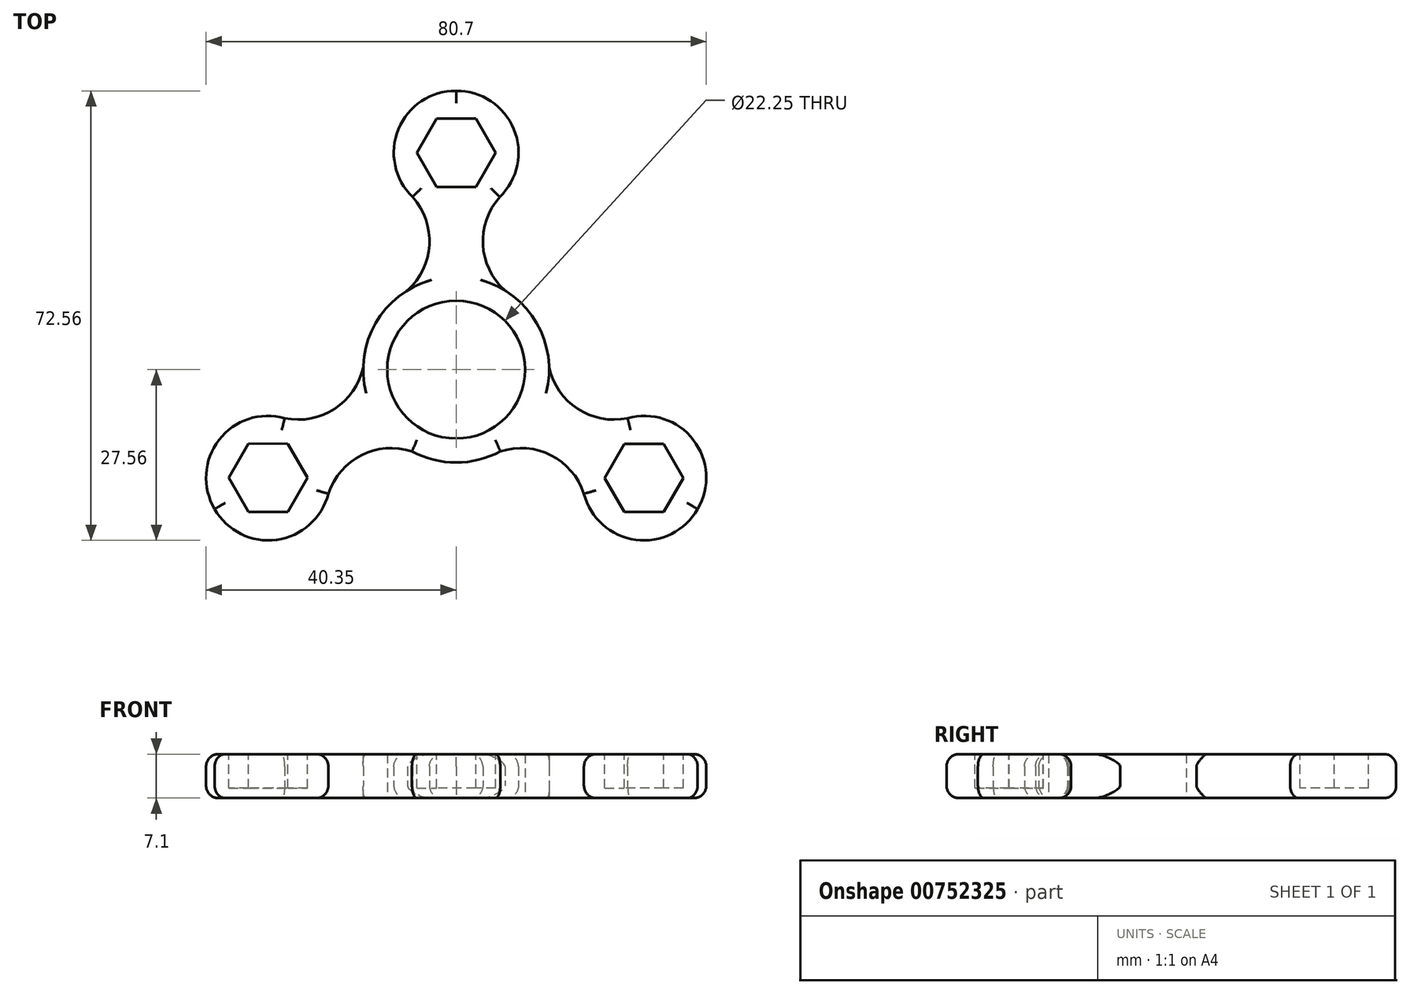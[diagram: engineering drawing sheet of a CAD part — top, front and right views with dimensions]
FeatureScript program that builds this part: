
annotation { "Feature Type Name" : "Feature", "Feature Type Description" : "" }
export const myFeature = defineFeature(function(context is Context, id is Id, definition is map)
    precondition{}
    {
        {
            var Q0;
            Q0=qCreatedBy(makeId("Top.planeOp"),FACE);
            var sketch = newSketch(context, id + "F0", { "sketchPlane" : qUnion([Q0])});
            skCircle(sketch, "E0", {"center": v(0, 0) * mm, "radius": 11.12 * mm});
            skCircle(sketch, "E1", {"center": v(0, 0) * mm, "radius": 15 * mm});
            skSolve(sketch);
        }
        {
            var Q0;
            Q0=qSketchRegion(id+"F0",true);
            extrude(context, id + "F1", {"entities" : qUnion([Q0]), "depth" : 7.1 * mm, "offsetDistance" : 25 * mm});
        }
        {
            var Q0;
            Q0=qCreatedBy(makeId("Top.planeOp"),FACE);
            var sketch = newSketch(context, id + "F2", { "sketchPlane" : qUnion([Q0])});
            skArc(sketch, "E2", {"start": v(7.04, 27.88) * mm, "mid": v(9.31, 38.82) * mm, "end": v(0, 45) * mm});
            skArc(sketch, "E3", {"start": v(7.04, 27.88) * mm, "mid": v(4.37, 19.6) * mm, "end": v(8.74, 12.07) * mm});
            skArc(sketch, "E4.MirrorCS", {"start": v(-7.04, 27.88) * mm, "mid": v(-9.31, 38.82) * mm, "end": v(0, 45) * mm});
            skArc(sketch, "E5.MirrorCS", {"start": v(-7.04, 27.88) * mm, "mid": v(-4.37, 19.6) * mm, "end": v(-8.74, 12.07) * mm});
            skArc(sketch, "E6", {"start": v(8.74, 12.07) * mm, "mid": v(0, 14.88) * mm, "end": v(-8.74, 12.07) * mm});
            skArc(sketch, "E7.1.0", {"start": v(-27.66, -7.84) * mm, "mid": v(-19.16, -6.01) * mm, "end": v(-14.82, 1.53) * mm});
            skArc(sketch, "E7.1.1", {"start": v(-20.62, -20.04) * mm, "mid": v(-14.78, -13.58) * mm, "end": v(-6.08, -13.6) * mm});
            skArc(sketch, "E7.1.2", {"start": v(-20.62, -20.04) * mm, "mid": v(-28.96, -27.47) * mm, "end": v(-38.97, -22.5) * mm});
            skArc(sketch, "E7.1.3", {"start": v(-27.66, -7.84) * mm, "mid": v(-38.27, -11.35) * mm, "end": v(-38.97, -22.5) * mm});
            skArc(sketch, "E7.1.4", {"start": v(-14.82, 1.53) * mm, "mid": v(-12.88, -7.44) * mm, "end": v(-6.08, -13.6) * mm});
            skArc(sketch, "E7.2.0", {"start": v(20.62, -20.04) * mm, "mid": v(14.78, -13.58) * mm, "end": v(6.08, -13.6) * mm});
            skArc(sketch, "E7.2.1", {"start": v(27.66, -7.84) * mm, "mid": v(19.16, -6.01) * mm, "end": v(14.82, 1.53) * mm});
            skArc(sketch, "E7.2.2", {"start": v(27.66, -7.84) * mm, "mid": v(38.27, -11.35) * mm, "end": v(38.97, -22.5) * mm});
            skArc(sketch, "E7.2.3", {"start": v(20.62, -20.04) * mm, "mid": v(28.96, -27.47) * mm, "end": v(38.97, -22.5) * mm});
            skArc(sketch, "E7.2.4", {"start": v(6.08, -13.6) * mm, "mid": v(12.88, -7.44) * mm, "end": v(14.82, 1.53) * mm});
            skPoint(sketch, "E7.center", {"position": v(0, 0) * mm});
            skSolve(sketch);
        }
        {
            var Q0;
            Q0=qSketchRegion(id+"F2",true);
            extrude(context, id + "F3", {"entities" : qUnion([Q0]), "operationType" : NewBodyOperationType.ADD, "depth" : 7.1 * mm, "offsetDistance" : 25 * mm});
        }
        {
            var Q0;
            Q0=makeQuery(id+"F3.opExtrude","CAP_EDGE",EDGE,{"disambiguationData":[OSD([sQuery(id+"F2.wireOp",EDGE,"E4.MirrorCS")])],"isStart":false});
            var Q1;
            Q1=makeQuery(id+"F3.opExtrude","CAP_EDGE",EDGE,{"disambiguationData":[OSD([sQuery(id+"F2.wireOp",EDGE,"E7.1.3")])],"isStart":false});
            var Q2;
            Q2=makeQuery(id+"F3.opExtrude","CAP_EDGE",EDGE,{"disambiguationData":[OSD([sQuery(id+"F2.wireOp",EDGE,"E7.2.3")])],"isStart":false});
            var Q3;
            {var subQ0=sQuery(id+"F0.wireOp",EDGE,"E1");var subQ1=sQuery(id+"F2.wireOp",EDGE,"E7.1.1");Q3=makeQuery(id+"F3.boolean.opBoolean","SPLIT",EDGE,{"disambiguationData":[TD([makeQuery(id+"F3.opExtrude","SWEPT_FACE",FACE,{"disambiguationData":[OSD([subQ1])]})])],"derivedFrom":makeQuery(id+"F1.opExtrude","CAP_EDGE",EDGE,{"disambiguationData":[OSD([subQ0])],"isStart":false})});}
            var Q4;
            {var subQ0=sQuery(id+"F2.wireOp",EDGE,"E3");var subQ1=sQuery(id+"F0.wireOp",EDGE,"E1");Q4=makeQuery(id+"F3.boolean.opBoolean","SPLIT",EDGE,{"disambiguationData":[TD([makeQuery(id+"F3.opExtrude","SWEPT_FACE",FACE,{"disambiguationData":[OSD([subQ0])]})])],"derivedFrom":makeQuery(id+"F1.opExtrude","CAP_EDGE",EDGE,{"disambiguationData":[OSD([subQ1])],"isStart":false})});}
            var Q5;
            {var subQ0=sQuery(id+"F2.wireOp",EDGE,"E5.MirrorCS");var subQ1=sQuery(id+"F0.wireOp",EDGE,"E1");Q5=makeQuery(id+"F3.boolean.opBoolean","SPLIT",EDGE,{"disambiguationData":[TD([makeQuery(id+"F3.opExtrude","SWEPT_FACE",FACE,{"disambiguationData":[OSD([subQ0])]})])],"derivedFrom":makeQuery(id+"F1.opExtrude","CAP_EDGE",EDGE,{"disambiguationData":[OSD([subQ1])],"isStart":false})});}
            var Q6;
            Q6=makeQuery(id+"F3.opExtrude","CAP_EDGE",EDGE,{"disambiguationData":[OSD([sQuery(id+"F2.wireOp",EDGE,"E7.1.3")])],"isStart":true});
            var Q7;
            Q7=makeQuery(id+"F3.opExtrude","CAP_EDGE",EDGE,{"disambiguationData":[OSD([sQuery(id+"F2.wireOp",EDGE,"E4.MirrorCS")])],"isStart":true});
            var Q8;
            Q8=makeQuery(id+"F3.opExtrude","CAP_EDGE",EDGE,{"disambiguationData":[OSD([sQuery(id+"F2.wireOp",EDGE,"E7.2.2")])],"isStart":true});
            var Q9;
            {var subQ0=sQuery(id+"F2.wireOp",EDGE,"E3");var subQ1=sQuery(id+"F0.wireOp",EDGE,"E1");Q9=makeQuery(id+"F3.boolean.opBoolean","SPLIT",EDGE,{"disambiguationData":[TD([makeQuery(id+"F3.opExtrude","SWEPT_FACE",FACE,{"disambiguationData":[OSD([subQ0])]})])],"derivedFrom":makeQuery(id+"F1.opExtrude","CAP_EDGE",EDGE,{"disambiguationData":[OSD([subQ1])],"isStart":true})});}
            var Q10;
            {var subQ0=sQuery(id+"F0.wireOp",EDGE,"E1");var subQ1=sQuery(id+"F2.wireOp",EDGE,"E7.1.1");Q10=makeQuery(id+"F3.boolean.opBoolean","SPLIT",EDGE,{"disambiguationData":[TD([makeQuery(id+"F3.opExtrude","SWEPT_FACE",FACE,{"disambiguationData":[OSD([subQ1])]})])],"derivedFrom":makeQuery(id+"F1.opExtrude","CAP_EDGE",EDGE,{"disambiguationData":[OSD([subQ0])],"isStart":true})});}
            var Q11;
            {var subQ0=sQuery(id+"F2.wireOp",EDGE,"E5.MirrorCS");var subQ1=sQuery(id+"F0.wireOp",EDGE,"E1");Q11=makeQuery(id+"F3.boolean.opBoolean","SPLIT",EDGE,{"disambiguationData":[TD([makeQuery(id+"F3.opExtrude","SWEPT_FACE",FACE,{"disambiguationData":[OSD([subQ0])]})])],"derivedFrom":makeQuery(id+"F1.opExtrude","CAP_EDGE",EDGE,{"disambiguationData":[OSD([subQ1])],"isStart":true})});}
            fillet(context, id + "F4", {"entities" : qUnion([Q0, Q1, Q2, Q3, Q4, Q5, Q6, Q7, Q8, Q9, Q10, Q11]), "radius" : 2 * mm, "tangentPropagation" : true, "allowEdgeOverflow" : false});
        }
        {
            var Q0;
            Q0=makeQuery(id+"F3.boolean.opBoolean","MERGE",FACE,{"derivedFrom":[makeQuery(id+"F1.opExtrude","CAP_FACE",FACE,{"disambiguationData":[OSD([sQuery(id+"F0.wireOp",EDGE,"E0"),sQuery(id+"F0.wireOp",EDGE,"E1")])],"isStart":false}),makeQuery(id+"F3.opExtrude","CAP_FACE",FACE,{"disambiguationData":[OSD([sQuery(id+"F2.wireOp",EDGE,"E2"),sQuery(id+"F2.wireOp",EDGE,"E3"),sQuery(id+"F2.wireOp",EDGE,"E4.MirrorCS"),sQuery(id+"F2.wireOp",EDGE,"E5.MirrorCS"),sQuery(id+"F2.wireOp",EDGE,"E6")])],"isStart":false}),makeQuery(id+"F3.opExtrude","CAP_FACE",FACE,{"disambiguationData":[OSD([sQuery(id+"F2.wireOp",EDGE,"E7.1.0"),sQuery(id+"F2.wireOp",EDGE,"E7.1.1"),sQuery(id+"F2.wireOp",EDGE,"E7.1.2"),sQuery(id+"F2.wireOp",EDGE,"E7.1.3"),sQuery(id+"F2.wireOp",EDGE,"E7.1.4")])],"isStart":false}),makeQuery(id+"F3.opExtrude","CAP_FACE",FACE,{"disambiguationData":[OSD([sQuery(id+"F2.wireOp",EDGE,"E7.2.0"),sQuery(id+"F2.wireOp",EDGE,"E7.2.1"),sQuery(id+"F2.wireOp",EDGE,"E7.2.2"),sQuery(id+"F2.wireOp",EDGE,"E7.2.3"),sQuery(id+"F2.wireOp",EDGE,"E7.2.4")])],"isStart":false})]});
            var sketch = newSketch(context, id + "F5", { "sketchPlane" : qUnion([Q0])});
            skCircle(sketch, "E8.cCircle", {"center": v(0, 35) * mm, "radius": 5.5 * mm, "construction": true});
            skLineSegment(sketch, "E8.0", {"start": v(3.18, 29.5) * mm, "end": v(-3.18, 29.5) * mm});
            skLineSegment(sketch, "E8.1", {"start": v(-3.18, 29.5) * mm, "end": v(-6.35, 35) * mm});
            skLineSegment(sketch, "E8.2", {"start": v(-6.35, 35) * mm, "end": v(-3.18, 40.5) * mm});
            skLineSegment(sketch, "E8.3", {"start": v(-3.18, 40.5) * mm, "end": v(3.18, 40.5) * mm});
            skLineSegment(sketch, "E8.4", {"start": v(3.18, 40.5) * mm, "end": v(6.35, 35) * mm});
            skLineSegment(sketch, "E8.5", {"start": v(6.35, 35) * mm, "end": v(3.18, 29.5) * mm});
            skPoint(sketch, "E8.0.midPoint", {"position": v(0, 29.5) * mm});
            skCircle(sketch, "E9.cCircle", {"center": v(-30.34, -17.45) * mm, "radius": 5.5 * mm, "construction": true});
            skLineSegment(sketch, "E9.0", {"start": v(-27.15, -11.96) * mm, "end": v(-23.99, -17.46) * mm});
            skLineSegment(sketch, "E9.1", {"start": v(-23.99, -17.46) * mm, "end": v(-27.17, -22.96) * mm});
            skLineSegment(sketch, "E9.2", {"start": v(-27.17, -22.96) * mm, "end": v(-33.52, -22.95) * mm});
            skLineSegment(sketch, "E9.3", {"start": v(-33.52, -22.95) * mm, "end": v(-36.69, -17.44) * mm});
            skLineSegment(sketch, "E9.4", {"start": v(-36.69, -17.44) * mm, "end": v(-33.5, -11.95) * mm});
            skLineSegment(sketch, "E9.5", {"start": v(-33.5, -11.95) * mm, "end": v(-27.15, -11.96) * mm});
            skPoint(sketch, "E9.0.midPoint", {"position": v(-25.57, -14.71) * mm});
            skCircle(sketch, "E10.cCircle", {"center": v(30.31, -17.5) * mm, "radius": 5.5 * mm, "construction": true});
            skLineSegment(sketch, "E10.0", {"start": v(23.96, -17.5) * mm, "end": v(27.14, -12) * mm});
            skLineSegment(sketch, "E10.1", {"start": v(27.14, -12) * mm, "end": v(33.49, -12) * mm});
            skLineSegment(sketch, "E10.2", {"start": v(33.49, -12) * mm, "end": v(36.66, -17.5) * mm});
            skLineSegment(sketch, "E10.3", {"start": v(36.66, -17.5) * mm, "end": v(33.49, -23) * mm});
            skLineSegment(sketch, "E10.4", {"start": v(33.49, -23) * mm, "end": v(27.14, -23) * mm});
            skLineSegment(sketch, "E10.5", {"start": v(27.14, -23) * mm, "end": v(23.96, -17.5) * mm});
            skPoint(sketch, "E10.0.midPoint", {"position": v(25.55, -14.75) * mm});
            skSolve(sketch);
        }
        {
            var Q0;
            Q0=qSketchRegion(id+"F5",true);
            extrude(context, id + "F6", {"entities" : qUnion([Q0]), "operationType" : NewBodyOperationType.REMOVE, "oppositeDirection" : true, "depth" : 5.5 * mm, "offsetDistance" : 25 * mm});
        }
    });
